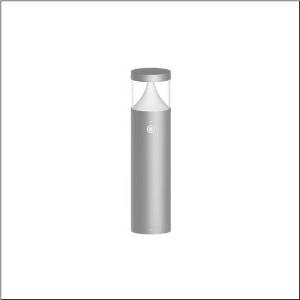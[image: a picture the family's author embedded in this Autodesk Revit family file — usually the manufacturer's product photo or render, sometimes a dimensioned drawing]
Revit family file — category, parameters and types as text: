
# Revit family: cl_31_poller_60_sensor_5cl434803
name_source: partatom
category: Lighting Fixtures
units: mm (PartAtom-declared; Revit-internal decimal feet)

## family parameters
Cut with Voids When Loaded = No
Host = Face
Light Source = No
Part Type = Normal
Room Calculation Point = No
Round Connector Dimension = Use Diameter
Shared = No

## types (1)
- --- (1 x LED, 1500 lm, 14 W, 3000K)
    Apparent Load = 14 VA
    CIE Flux Codes = 19 66 88 92 100
    Color Rendering = 80
    Color Temperature = 3000K
    Default Elevation = 1800 mm
    Description = CL 31 Bollard 60 Sensor, bollard luminaire, primary light control with lens, of PC, primary optical cover: cover panel, of PC, transparent, secondary light control with reflector, of PC, primary light characteristic: asymmetric, LED, rated luminous flux: 1.500lm, luminous efficacy: 107lm/W, light colour: 830, colour temperature: 3000K, control gear: DALI, with terminal, 5-pole, max. 2.5mm², mains connection: 220..240V, AC, 50/60Hz, rated input power: 14W, luminaire housing, of aluminium, powder-coated, Siteco® metallic grey, diameter: 170mm, height: 600mm, PIR sensor, protection rating (complete): IP65, insulation class (complete): insulation class I (protective earthing), certification: CE, ENEC, impact resistance: IK08, permissible operating ambient temperature for outdoor applications: -20..+50°C, packaging unit: 1 piece
    Height = 200 mm  [stored 0.656168 ft]
    Lamp = 1 x LED
    Lamp Light Flux = 1500 lm
    Lamp Power = 14 W
    Lamp count = 1
    Length = 170 mm  [stored 0.557743 ft]
    Luminous efficacy = 107 lm/W
    Manufacturer = Siteco
    ModVariant = No
    Model = 5CL434803
    Mounting Place = Floor
    Mounting Type = Freestanding
    Number of Poles = 1
    OnlyDefault = Yes
    Power Factor = 1
    Product Name = CL 31 Poller 60 Sensor
    Product group = bollard luminaire
    ProductGroupID = 1304
    Protection Class = Protection class I
    Protection Degree = IP 65
    RLX_Detail_Level = 1
    RLX_Emergency_Light_Flux = 0 lm
    RLX_Emergency_Type = 0
    RLX_Emergency_Type_DB = No
    RlxData = <blob elided: 64465 chars, md5=7535fafb>
    Socket = socket
    Standby Power = 0 W
    System Light Flux = 1500 lm
    System Power = 14 W
    Type Comments = factory setting: luminous flux: 100 % | dim-lin: 254 | 350 mA
    Type Image = l_1006901.jpg
    URL = http://relux.com
    VarID = @adj_195162
    Voltage = 0 V
    Weight = 0.00 kg
    Width = 0 mm  [stored 0 ft]

note: [stored X ft] marks values corroborated as IEEE doubles in the binary element streams (Revit-internal decimal feet)

## geometry (parser evidence)
native form markers: Blend x4, Sweep x13
no freeform markers — native parametric forms only
